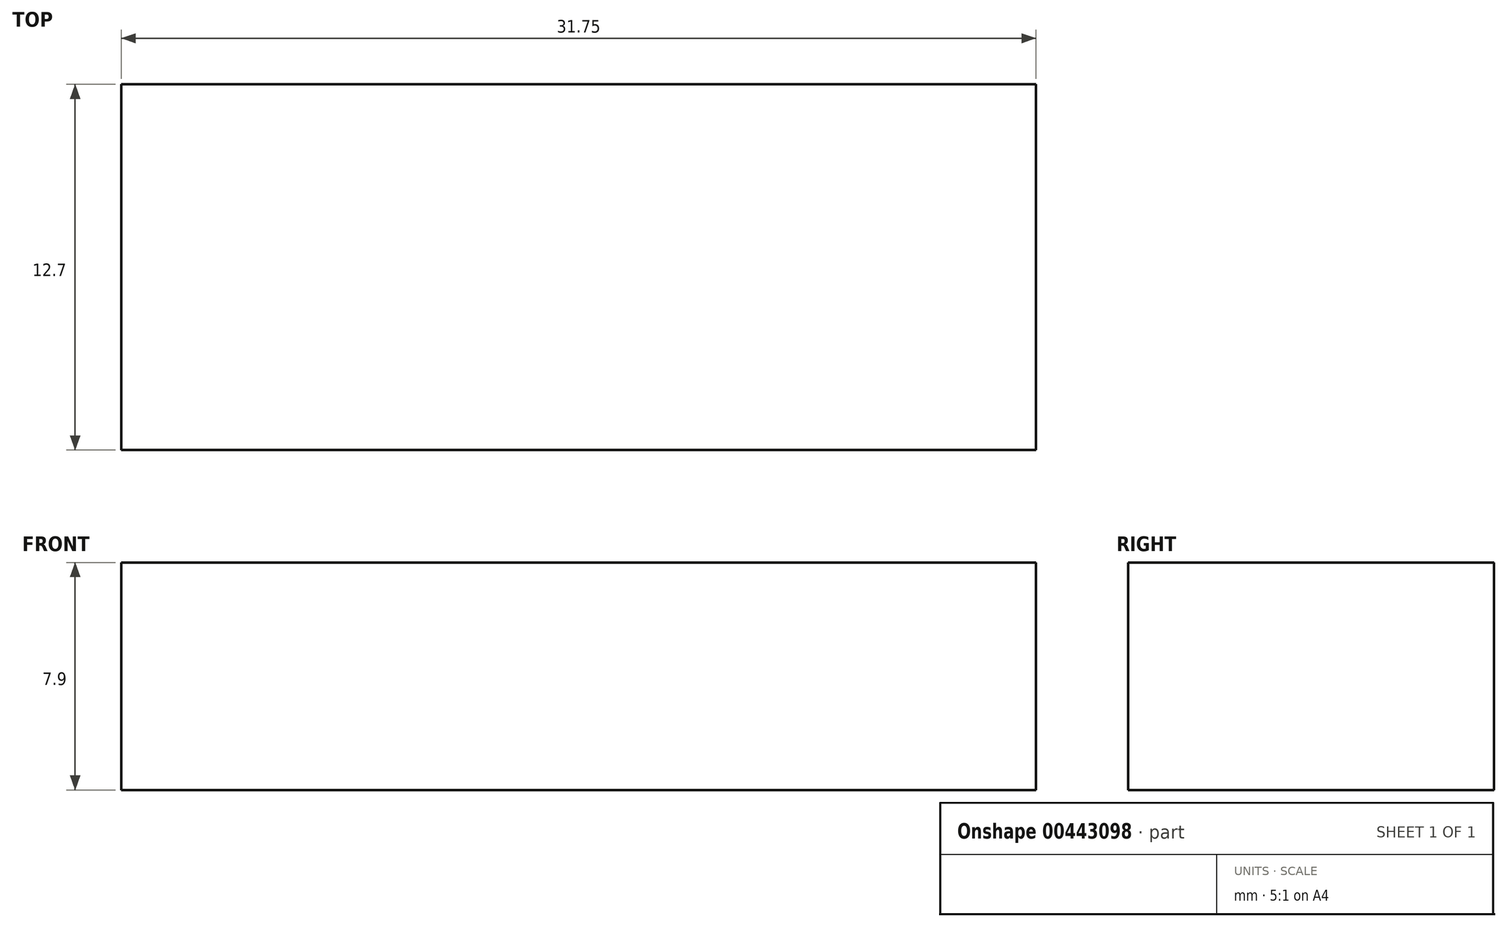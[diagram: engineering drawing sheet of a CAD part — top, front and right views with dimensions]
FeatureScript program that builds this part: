
annotation { "Feature Type Name" : "Feature", "Feature Type Description" : "" }
export const myFeature = defineFeature(function(context is Context, id is Id, definition is map)
    precondition{}
    {
        {
            var Q0;
            Q0=qCreatedBy(makeId("Top.planeOp"),FACE);
            var sketch = newSketch(context, id + "F0", { "sketchPlane" : qUnion([Q0])});
            skLineSegment(sketch, "E0.bottom", {"start": v(0, 0) * mm, "end": v(-38.1, 0) * mm});
            skLineSegment(sketch, "E0.top", {"start": v(0, 20.32) * mm, "end": v(-38.1, 20.32) * mm});
            skLineSegment(sketch, "E0.left", {"start": v(0, 0) * mm, "end": v(0, 20.32) * mm});
            skLineSegment(sketch, "E0.right", {"start": v(-38.1, 0) * mm, "end": v(-38.1, 20.32) * mm});
            skLineSegment(sketch, "E1.bottom", {"start": v(-31.75, 12.7) * mm, "end": v(0, 12.7) * mm});
            skLineSegment(sketch, "E1.top", {"start": v(-31.75, 0) * mm, "end": v(0, 0) * mm});
            skLineSegment(sketch, "E1.left", {"start": v(-31.75, 12.7) * mm, "end": v(-31.75, 0) * mm});
            skLineSegment(sketch, "E1.right", {"start": v(0, 12.7) * mm, "end": v(0, 0) * mm});
            skSolve(sketch);
        }
        {
            var Q0;
            Q0=makeQuery(id+"F0.imprint","IMPRINT",FACE,{"disambiguationData":[TD([[makeQuery(id+"F0.imprint","IMPRINT",EDGE,{"derivedFrom":sQuery(id+"F0.wireOp",EDGE,"E0.bottom")}),-1.0]])]});
            extrude(context, id + "F1", {"entities" : qUnion([Q0]), "depth" : 7.9 * mm});
        }
        {
            var Q0;
            Q0=makeQuery(id+"F1.opExtrude","CAP_FACE",FACE,{"disambiguationData":[OSD([sQuery(id+"F0.wireOp",EDGE,"E0.bottom"),sQuery(id+"F0.wireOp",EDGE,"E0.top"),sQuery(id+"F0.wireOp",EDGE,"E0.left"),sQuery(id+"F0.wireOp",EDGE,"E0.right"),sQuery(id+"F0.wireOp",EDGE,"E1.bottom"),sQuery(id+"F0.wireOp",EDGE,"E1.left")])],"isStart":true});
            var sketch = newSketch(context, id + "F2", { "sketchPlane" : qUnion([Q0])});
            skCircle(sketch, "E2", {"center": v(-8, -16.51) * mm, "radius": 1.5 * mm});
            skCircle(sketch, "E3", {"center": v(-13.25, -16.51) * mm, "radius": 1.5 * mm});
            skPoint(sketch, "E4", {"position": v(0, -16.51) * mm});
            skLineSegment(sketch, "E5", {"start": v(0, -16.51) * mm, "end": v(-17.36, -16.51) * mm});
            skSolve(sketch);
        }
        {
            var Q0;
            Q0=qSketchRegion(id+"F2",true);
            extrude(context, id + "F3", {"entities" : qUnion([Q0]), "operationType" : NewBodyOperationType.REMOVE, "oppositeDirection" : true, "depth" : 25.4 * mm});
        }
    });
